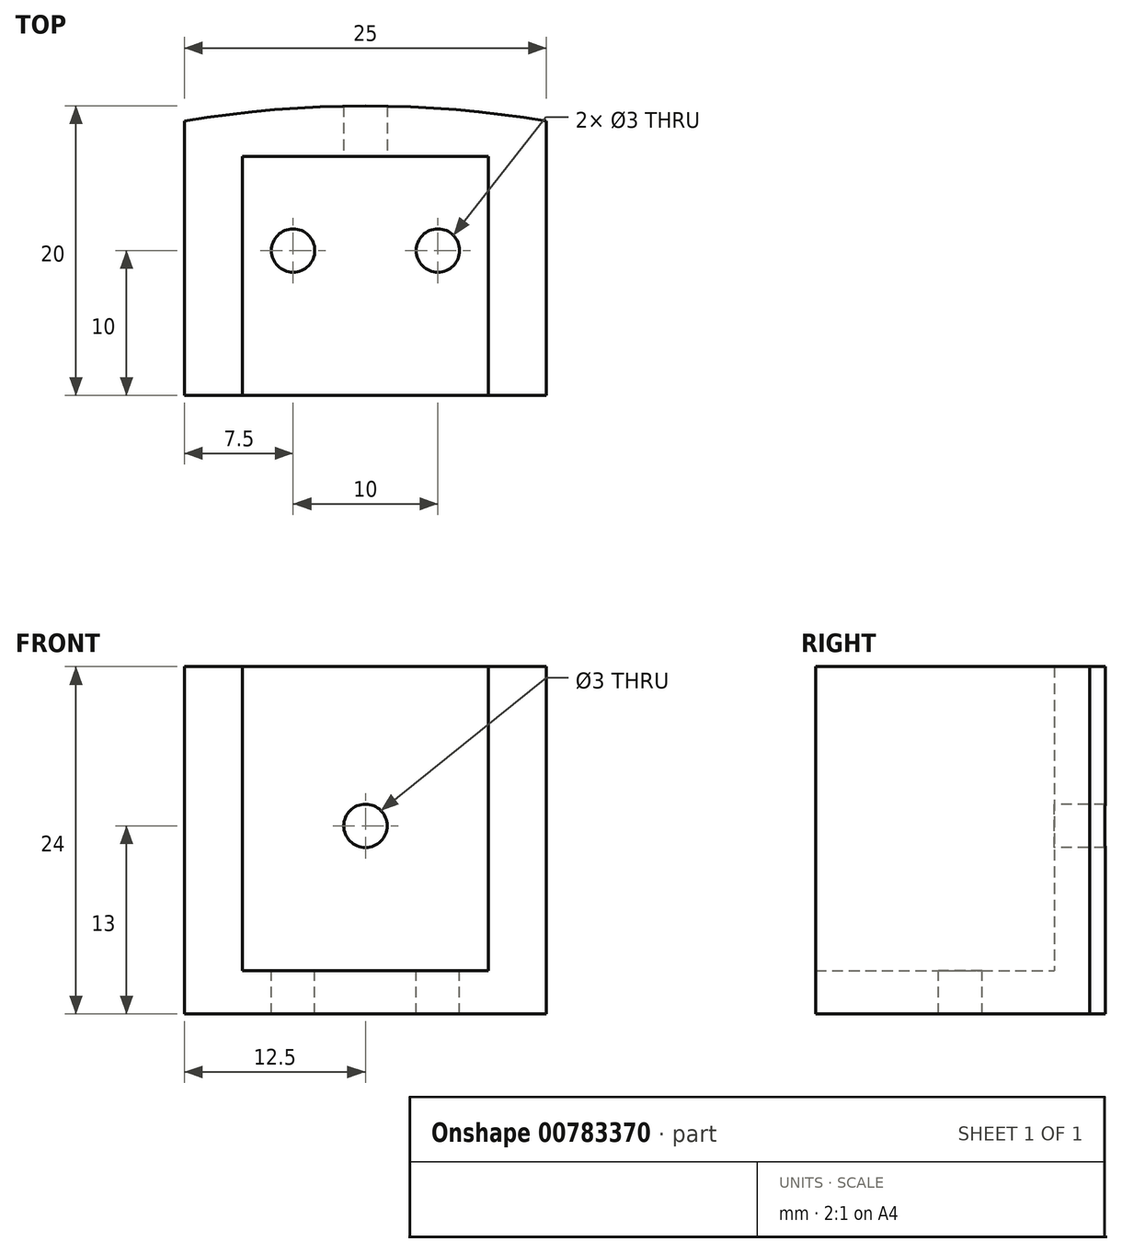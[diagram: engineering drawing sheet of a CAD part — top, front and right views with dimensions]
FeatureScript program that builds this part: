
annotation { "Feature Type Name" : "Feature", "Feature Type Description" : "" }
export const myFeature = defineFeature(function(context is Context, id is Id, definition is map)
    precondition{}
    {
        {
            var Q0;
            Q0=qCreatedBy(makeId("Top.planeOp"),FACE);
            var sketch = newSketch(context, id + "F0", { "sketchPlane" : qUnion([Q0])});
            skArc(sketch, "E0", {"start": v(12.5, 73.7) * mm, "mid": v(0, 74.75) * mm, "end": v(-12.5, 73.7) * mm});
            skLineSegment(sketch, "E1", {"start": v(-12.5, 54.75) * mm, "end": v(12.5, 54.75) * mm});
            skLineSegment(sketch, "E2", {"start": v(12.5, 54.75) * mm, "end": v(12.5, 73.7) * mm});
            skLineSegment(sketch, "E3", {"start": v(-12.5, 54.75) * mm, "end": v(-12.5, 73.7) * mm});
            skPoint(sketch, "E4.end.orphan", {"position": v(0, 54.75) * mm});
            skPoint(sketch, "E4.start.orphan", {"position": v(0, 74.75) * mm});
            skLineSegment(sketch, "E5", {"start": v(12.5, 54.75) * mm, "end": v(8.38, 54.75) * mm});
            skSolve(sketch);
        }
        {
            var Q0;
            Q0=makeQuery(id+"F0.imprint","IMPRINT",FACE,{"disambiguationData":[TD([[makeQuery(id+"F0.imprint","IMPRINT",EDGE,{"derivedFrom":sQuery(id+"F0.wireOp",EDGE,"E0")}),1.0]])]});
            extrude(context, id + "F1", {"entities" : qUnion([Q0]), "depth" : 3 * mm, "offsetDistance" : 25 * mm});
        }
        {
            var Q0;
            Q0=makeQuery(id+"F1.opExtrude","CAP_FACE",FACE,{"disambiguationData":[OSD([sQuery(id+"F0.wireOp",EDGE,"E0"),sQuery(id+"F0.wireOp",EDGE,"E1"),sQuery(id+"F0.wireOp",EDGE,"E2"),sQuery(id+"F0.wireOp",EDGE,"E3"),sQuery(id+"F0.wireOp",EDGE,"E5")])],"isStart":false});
            var sketch = newSketch(context, id + "F2", { "sketchPlane" : qUnion([Q0])});
            skLineSegment(sketch, "E6", {"start": v(-12.5, 54.75) * mm, "end": v(-8.5, 54.75) * mm});
            skLineSegment(sketch, "E7", {"start": v(-8.5, 54.75) * mm, "end": v(-8.5, 71.25) * mm});
            skLineSegment(sketch, "E8", {"start": v(12.5, 54.75) * mm, "end": v(8.5, 54.75) * mm});
            skLineSegment(sketch, "E9", {"start": v(8.5, 54.75) * mm, "end": v(8.5, 71.25) * mm});
            skLineSegment(sketch, "E10", {"start": v(-8.5, 71.25) * mm, "end": v(8.5, 71.25) * mm});
            skSolve(sketch);
        }
        {
            var Q0;
            Q0=makeQuery(id+"F2.imprint","IMPRINT",FACE,{"disambiguationData":[TD([[makeQuery(id+"F2.imprint","IMPRINT",EDGE,{"derivedFrom":sQuery(id+"F2.wireOp",EDGE,"E6")}),1.0]])]});
            extrude(context, id + "F3", {"entities" : qUnion([Q0]), "operationType" : NewBodyOperationType.ADD, "depth" : 21 * mm, "offsetDistance" : 25 * mm});
        }
        {
            var Q0;
            Q0=makeQuery(id+"F1.opExtrude","CAP_FACE",FACE,{"disambiguationData":[OSD([sQuery(id+"F0.wireOp",EDGE,"E0"),sQuery(id+"F0.wireOp",EDGE,"E1"),sQuery(id+"F0.wireOp",EDGE,"E2"),sQuery(id+"F0.wireOp",EDGE,"E3"),sQuery(id+"F0.wireOp",EDGE,"E5")])],"isStart":false});
            var sketch = newSketch(context, id + "F4", { "sketchPlane" : qUnion([Q0])});
            skLineSegment(sketch, "E11", {"start": v(0, 54.75) * mm, "end": v(0, 64.75) * mm});
            skLineSegment(sketch, "E12", {"start": v(-5, 64.75) * mm, "end": v(5, 64.75) * mm});
            skCircle(sketch, "E13", {"center": v(-5, 64.75) * mm, "radius": 1.5 * mm});
            skCircle(sketch, "E14", {"center": v(5, 64.75) * mm, "radius": 1.5 * mm});
            skSolve(sketch);
        }
        {
            var Q0;
            Q0=makeQuery(id+"F4.imprint","IMPRINT",FACE,{"disambiguationData":[TD([[makeQuery(id+"F4.imprint","IMPRINT",EDGE,{"derivedFrom":sQuery(id+"F4.wireOp",EDGE,"E14")}),1.0]])]});
            var Q1;
            Q1=makeQuery(id+"F4.imprint","IMPRINT",FACE,{"disambiguationData":[TD([[makeQuery(id+"F4.imprint","IMPRINT",EDGE,{"derivedFrom":sQuery(id+"F4.wireOp",EDGE,"E13")}),1.0]])]});
            var Q2;
            Q2=sQuery(id+"F4.wireOp",EDGE,"E13");
            var Q3;
            Q3=sQuery(id+"F4.wireOp",EDGE,"E14");
            extrude(context, id + "F5", {"entities" : qUnion([Q0, Q1]), "operationType" : NewBodyOperationType.REMOVE, "surfaceEntities" : qUnion([Q2, Q3]), "oppositeDirection" : true, "depth" : 4 * mm, "offsetDistance" : 25 * mm});
        }
        {
            var Q0;
            Q0=makeQuery(id+"F3.opExtrude","SWEPT_FACE",FACE,{"disambiguationData":[OSD([sQuery(id+"F2.wireOp",EDGE,"E10")])]});
            var sketch = newSketch(context, id + "F6", { "sketchPlane" : qUnion([Q0])});
            skLineSegment(sketch, "E15", {"start": v(0, 24) * mm, "end": v(0, 13) * mm});
            skCircle(sketch, "E16", {"center": v(0, 13) * mm, "radius": 1.5 * mm});
            skSolve(sketch);
        }
        {
            var Q0;
            Q0=makeQuery(id+"F6.imprint","IMPRINT",FACE,{"disambiguationData":[TD([[makeQuery(id+"F6.imprint","IMPRINT",EDGE,{"derivedFrom":sQuery(id+"F6.wireOp",EDGE,"E16")}),1.0]])]});
            var Q1;
            Q1=sQuery(id+"F6.wireOp",EDGE,"E16");
            extrude(context, id + "F7", {"entities" : qUnion([Q0]), "operationType" : NewBodyOperationType.REMOVE, "surfaceOperationType" : NewSurfaceOperationType.ADD, "surfaceEntities" : qUnion([Q1]), "depth" : -5 * mm, "offsetDistance" : 25 * mm});
        }
    });
